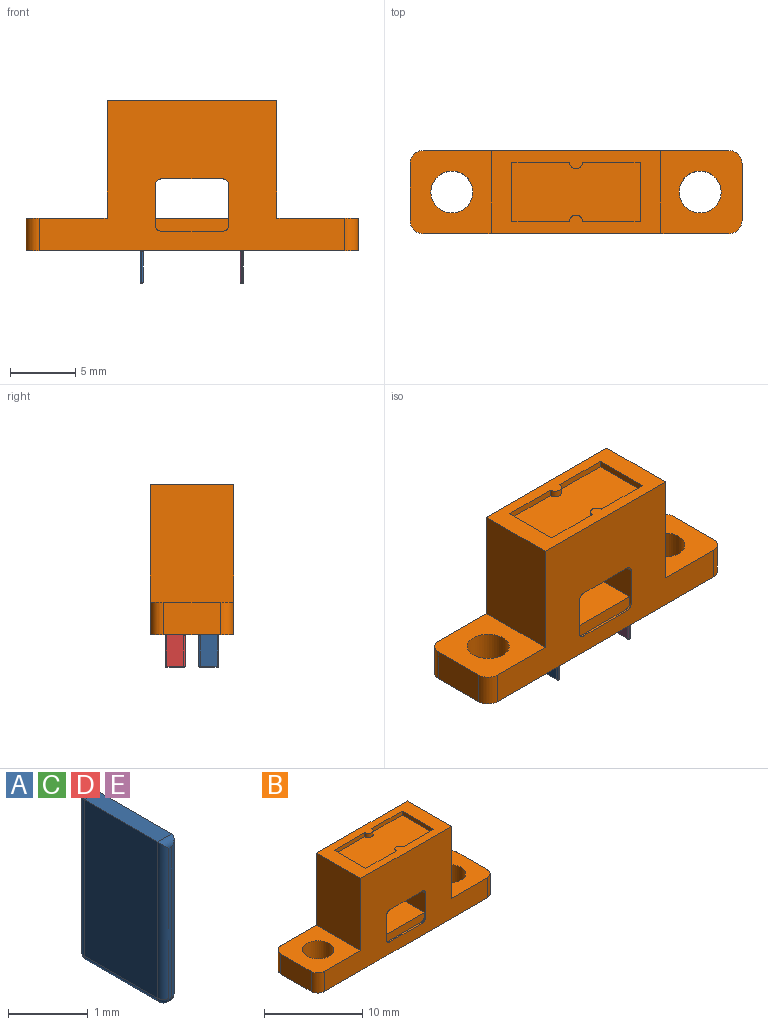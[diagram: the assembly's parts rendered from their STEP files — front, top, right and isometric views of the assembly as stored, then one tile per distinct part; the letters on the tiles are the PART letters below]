
ASSEMBLY  parts=5 mates=1
PART A: 20 faces, bbox 0.3x1.5x2.5 mm
  f0: plane 2.4x1.3mm, normal (-1,0,0), area 3.1mm2, adj f5,f9,f14,f19
  f1: plane 2.3x0.05mm, normal (0,1,0), area 0.1mm2, adj f15,f16,f18,f19
  f2: plane 2.4x1.3mm, normal (1,0,0), area 3.1mm2, adj f5,f6,f11,f16
  f3: plane 2.3x0.05mm, normal (0,-1,0), area 0.1mm2, adj f6,f7,f9,f10
  f4: plane 1.3x0.05mm, normal (0,0,-1), area 0.1mm2, adj f10,f11,f14,f15
  f5: plane 1.3x0.25mm, normal (0,0,1), area 0.3mm2, adj f0,f2,f7,f18
  f6: cylinder r=0.1mm len=2.4mm, axis (0,0,1), area 0.4mm2, adj f2,f3,f7,f8
  f7: cylinder r=0.1mm len=0.25mm, axis (-1,0,0), area 0mm2, adj f3,f5,f6,f9
  f8: sphere r=0.1mm, area 0mm2, adj f6,f10,f11
  f9: cylinder r=0.1mm len=2.4mm, axis (0,0,-1), area 0.4mm2, adj f0,f3,f7,f12
  f10: cylinder r=0.1mm len=0.1mm, axis (1,0,0), area 0mm2, adj f3,f4,f8,f12
  f11: cylinder r=0.1mm len=1.3mm, axis (0,1,0), area 0.2mm2, adj f2,f4,f8,f13
  f12: sphere r=0.1mm, area 0mm2, adj f9,f10,f14
  f13: sphere r=0.1mm, area 0mm2, adj f11,f15,f16
  f14: cylinder r=0.1mm len=1.3mm, axis (0,-1,0), area 0.2mm2, adj f0,f4,f12,f17
  f15: cylinder r=0.1mm len=0.1mm, axis (-1,0,0), area 0mm2, adj f1,f4,f13,f17
  f16: cylinder r=0.1mm len=2.4mm, axis (0,0,-1), area 0.4mm2, adj f1,f2,f13,f18
  f17: sphere r=0.1mm, area 0mm2, adj f14,f15,f19
  f18: cylinder r=0.1mm len=0.25mm, axis (1,0,0), area 0mm2, adj f1,f5,f16,f19
  f19: cylinder r=0.1mm len=2.4mm, axis (0,0,1), area 0.4mm2, adj f0,f1,f17,f18
PART B: 39 faces, bbox 25.4x6.4x11.5 mm
  f0: plane 4.65x0.18mm, normal (0,0,1), area 0.8mm2, adj f1,f2,f5,f37
  f1: cylinder r=0.5mm len=0.5mm, axis (0,-1,0), area 0.1mm2, adj f0,f5,f31,f37
  f2: cylinder r=0.5mm len=0.5mm, axis (0,-1,0), area 0.1mm2, adj f0,f5,f35,f37
  f3: plane 13x6.35mm, normal (0,0,1), area 38.7mm2, adj f5,f7,f13,f14,f15,f16,f17,f18
  f4: plane 6.35x6.2mm, normal (0,0,1), area 30.9mm2, adj f5,f6,f7,f10,f14,f26,f27
  f5: plane 23.4x11.5mm, normal (0,-1,0), area 153.1mm2, adj f0,f1,f2,f3,f4,f11,f12,f13
  f6: plane 4.35x2.5mm, normal (1,0,0), area 10.9mm2, adj f4,f12,f26,f27
  f7: plane 23.4x11.5mm, normal (0,1,0), area 153.1mm2, adj f3,f4,f11,f12,f13,f14,f24,f27
  f8: plane 4.35x2.5mm, normal (-1,0,0), area 10.9mm2, adj f11,f12,f24,f25
  f9: cylinder r=1.6mm len=3.2mm, axis (0,0,-1), area 25.1mm2, adj f11,f12
  f10: cylinder r=1.6mm len=3.2mm, axis (0,0,-1), area 25.1mm2, adj f4,f12
  f11: plane 6.35x6.2mm, normal (0,0,1), area 30.9mm2, adj f5,f7,f8,f9,f13,f24,f25
  f12: plane 25.4x6.35mm, normal (0,0,-1), area 144.3mm2, adj f5,f6,f7,f8,f9,f10,f24,f25
  f13: plane 9x6.35mm, normal (-1,0,0), area 57.1mm2, adj f3,f5,f7,f11
  f14: plane 9x6.35mm, normal (1,0,0), area 57.1mm2, adj f3,f4,f5,f7
  f15: plane 4.55x0.5mm, normal (-1,0,0), area 2.3mm2, adj f3,f16,f22,f23
  f16: plane 4.4x0.5mm, normal (0,-1,0), area 2.2mm2, adj f3,f15,f17,f23
  f17: cylinder r=0.5mm len=1mm, axis (0,0,1), area 0.8mm2, adj f3,f16,f18,f23
  f18: plane 4.4x0.5mm, normal (0,-1,0), area 2.2mm2, adj f3,f17,f19,f23
  f19: plane 4.55x0.5mm, normal (1,0,0), area 2.3mm2, adj f3,f18,f20,f23
  f20: plane 4.4x0.5mm, normal (0,1,0), area 2.2mm2, adj f3,f19,f21,f23
  f21: cylinder r=0.5mm len=1mm, axis (0,0,1), area 0.8mm2, adj f3,f20,f22,f23
  f22: plane 4.4x0.5mm, normal (0,1,0), area 2.2mm2, adj f3,f15,f21,f23
  f23: plane 9.8x4.55mm, normal (0,0,1), area 43.8mm2, adj f15,f16,f17,f18,f19,f20,f21,f22
  f24: cylinder r=1mm len=2.5mm, axis (0,0,1), area 3.9mm2, adj f7,f8,f11,f12
  f25: cylinder r=1mm len=2.5mm, axis (0,0,-1), area 3.9mm2, adj f5,f8,f11,f12
  f26: cylinder r=1mm len=2.5mm, axis (0,0,1), area 3.9mm2, adj f4,f5,f6,f12
  f27: cylinder r=1mm len=2.5mm, axis (0,0,-1), area 3.9mm2, adj f4,f6,f7,f12
  f28: cylinder r=0.5mm len=6.35mm, axis (0,-1,0), area 5mm2, adj f5,f7,f29,f35
  f29: plane 6.35x4.65mm, normal (0,0,-1), area 29.5mm2, adj f5,f7,f28,f30
  f30: cylinder r=0.5mm len=6.35mm, axis (0,-1,0), area 5mm2, adj f5,f7,f29,f31
  f31: plane 6.35x3mm, normal (1,0,0), area 16.1mm2, adj f1,f5,f7,f30,f32,f36,f37,f38
  f32: cylinder r=0.5mm len=0.5mm, axis (0,-1,0), area 0.1mm2, adj f7,f31,f33,f38
  f33: plane 4.65x0.18mm, normal (0,0,1), area 0.8mm2, adj f7,f32,f34,f38
  f34: cylinder r=0.5mm len=0.5mm, axis (0,-1,0), area 0.1mm2, adj f7,f33,f35,f38
  f35: plane 6.35x3mm, normal (-1,0,0), area 16.1mm2, adj f2,f5,f7,f28,f34,f36,f37,f38
  f36: plane 6x5.65mm, normal (0,0,1), area 33.9mm2, adj f31,f35,f37,f38
  f37: plane 5.65x1mm, normal (0,-1,0), area 5.5mm2, adj f0,f1,f2,f31,f35,f36
  f38: plane 5.65x1mm, normal (0,1,0), area 5.5mm2, adj f31,f32,f33,f34,f35,f36
PART C: same geometry as A
PART D: same geometry as A
PART E: same geometry as A
PLACE A t=(-12.11,-1.57,-0.44)mm
PLACE B t=(-4.45,0.97,-0.44)mm
PLACE C t=(-4.45,0.97,-0.44)mm
PLACE D t=(-12.11,0.97,-0.44)mm
PLACE E t=(-4.45,-1.57,-0.44)mm
MATE fastened C.f5 <-> B.f12  axis (0,0,1) through (-0.64,2.24,-0.44)mm
